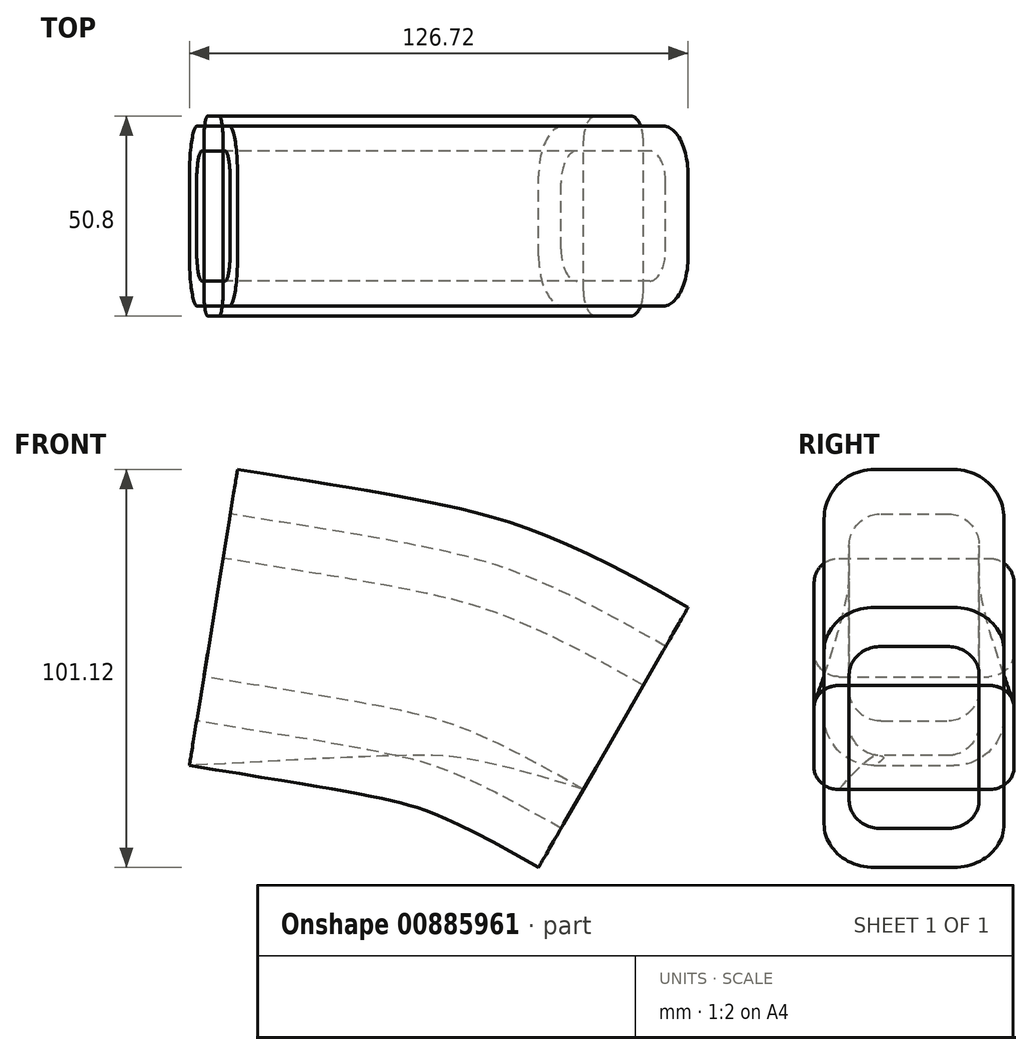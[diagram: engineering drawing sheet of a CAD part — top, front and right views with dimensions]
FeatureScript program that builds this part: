
annotation { "Feature Type Name" : "Feature", "Feature Type Description" : "" }
export const myFeature = defineFeature(function(context is Context, id is Id, definition is map)
    precondition{}
    {
        {
            var Q0;
            Q0=qCreatedBy(makeId("Right.planeOp"),FACE);
            var sketch = newSketch(context, id + "F0", { "sketchPlane" : qUnion([Q0])});
            skLineSegment(sketch, "E0", {"start": v(0, 0) * mm, "end": v(12.7, 0) * mm, "construction": true});
            skSolve(sketch);
        }
        {
            var Q0;
            Q0=qCreatedBy(makeId("Front.planeOp"),FACE);
            var sketch = newSketch(context, id + "F1", { "sketchPlane" : qUnion([Q0])});
            skLineSegment(sketch, "E1", {"start": v(0, 0) * mm, "end": v(0, 45.51) * mm});
            skFitSpline(sketch, "E2", {"points": [v(0, 0) * mm, v(-49.33, 21.4) * mm, v(-101.6, 30.48) * mm], "startDerivative": vector(-161.46, 92.87) * mm, "endDerivative": vector(-157.97, 25.7) * mm});
            skLineSegment(sketch, "E3", {"start": v(-101.6, 30.48) * mm, "end": v(0, 30.48) * mm, "construction": true});
            skPoint(sketch, "E3.endSnap0", {"position": v(0, 22.76) * mm});
            skSolve(sketch);
        }
        {
            var Q0;
            Q0=sQuery(id+"F1.wireOp",VERTEX,"E2.end");
            var Q1;
            Q1=sQuery(id+"F1.wireOp",EDGE,"E2");
            cPlane(context, id + "F2", {"entities" : qUnion([Q0, Q1]), "cplaneType" : CPlaneType.CURVE_POINT, "offset" : 25.4 * mm, "width" : 152.4 * mm, "height" : 152.4 * mm});
        }
        {
            var Q0;
            Q0=sQuery(id+"F1.wireOp",EDGE,"E2");
            var Q1;
            Q1=sQuery(id+"F1.wireOp",VERTEX,"E2.1.internal");
            cPlane(context, id + "F3", {"entities" : qUnion([Q0, Q1]), "cplaneType" : CPlaneType.CURVE_POINT, "offset" : 25.4 * mm, "width" : 152.4 * mm, "height" : 152.4 * mm});
        }
        {
            var Q0;
            Q0=sQuery(id+"F1.wireOp",EDGE,"E2");
            var Q1;
            Q1=sQuery(id+"F0.wireOp",VERTEX,"E0.start");
            cPlane(context, id + "F4", {"entities" : qUnion([Q0, Q1]), "cplaneType" : CPlaneType.CURVE_POINT, "offset" : 25.4 * mm, "width" : 152.4 * mm, "height" : 152.4 * mm});
        }
        {
            var Q0;
            Q0=qCreatedBy(id+"F4.planeOp",FACE);
            var sketch = newSketch(context, id + "F5", { "sketchPlane" : qUnion([Q0])});
            skLineSegment(sketch, "E4", {"start": v(0, 0) * mm, "end": v(0, 15.24) * mm, "construction": true});
            skLineSegment(sketch, "E5", {"start": v(0, 0) * mm, "end": v(25.4, 0) * mm, "construction": true});
            skLineSegment(sketch, "E6.bottom", {"start": v(19.05, -15.24) * mm, "end": v(-19.05, -15.24) * mm});
            skLineSegment(sketch, "E6.top", {"start": v(19.05, 15.24) * mm, "end": v(-19.05, 15.24) * mm});
            skLineSegment(sketch, "E6.left", {"start": v(25.4, -8.9) * mm, "end": v(25.4, 8.89) * mm});
            skLineSegment(sketch, "E6.right", {"start": v(-25.4, -8.89) * mm, "end": v(-25.4, 8.9) * mm});
            skPoint(sketch, "E7.visualSharp", {"position": v(25.4, -15.24) * mm});
            skArc(sketch, "E7.filletArc", {"start": v(19.05, -15.24) * mm, "mid": v(23.54, -13.38) * mm, "end": v(25.4, -8.9) * mm});
            skPoint(sketch, "E8.visualSharp", {"position": v(25.4, 15.24) * mm});
            skArc(sketch, "E8.filletArc", {"start": v(25.4, 8.89) * mm, "mid": v(23.54, 13.38) * mm, "end": v(19.05, 15.24) * mm});
            skPoint(sketch, "E9.visualSharp", {"position": v(-25.4, 15.24) * mm});
            skArc(sketch, "E9.filletArc", {"start": v(-19.05, 15.24) * mm, "mid": v(-23.54, 13.38) * mm, "end": v(-25.4, 8.9) * mm});
            skPoint(sketch, "E10.visualSharp", {"position": v(-25.4, -15.24) * mm});
            skArc(sketch, "E10.filletArc", {"start": v(-25.4, -8.89) * mm, "mid": v(-23.54, -13.38) * mm, "end": v(-19.05, -15.24) * mm});
            skSolve(sketch);
        }
        {
            var Q0;
            Q0=qCreatedBy(id+"F3.planeOp",FACE);
            var sketch = newSketch(context, id + "F6", { "sketchPlane" : qUnion([Q0])});
            skLineSegment(sketch, "E11", {"start": v(0, 10.28) * mm, "end": v(-16.51, 10.28) * mm, "construction": true});
            skLineSegment(sketch, "E12", {"start": v(0, 10.28) * mm, "end": v(0, 36.95) * mm, "construction": true});
            skLineSegment(sketch, "E13.bottom", {"start": v(8.38, 36.95) * mm, "end": v(-8.38, 36.95) * mm});
            skLineSegment(sketch, "E13.top", {"start": v(8.38, -16.4) * mm, "end": v(-8.38, -16.4) * mm});
            skLineSegment(sketch, "E13.left", {"start": v(16.5, 28.82) * mm, "end": v(16.5, -8.26) * mm});
            skLineSegment(sketch, "E13.right", {"start": v(-16.51, 28.82) * mm, "end": v(-16.51, -8.26) * mm});
            skPoint(sketch, "E14.visualSharp", {"position": v(16.5, 36.95) * mm});
            skArc(sketch, "E14.filletArc", {"start": v(16.51, 28.82) * mm, "mid": v(14.13, 34.57) * mm, "end": v(8.38, 36.95) * mm});
            skPoint(sketch, "E15.visualSharp", {"position": v(16.51, -16.4) * mm});
            skArc(sketch, "E15.filletArc", {"start": v(8.38, -16.4) * mm, "mid": v(14.13, -14.01) * mm, "end": v(16.51, -8.26) * mm});
            skPoint(sketch, "E16.visualSharp", {"position": v(-16.51, -16.4) * mm});
            skArc(sketch, "E16.filletArc", {"start": v(-16.51, -8.26) * mm, "mid": v(-14.13, -14.01) * mm, "end": v(-8.38, -16.4) * mm});
            skPoint(sketch, "E17.visualSharp", {"position": v(-16.51, 36.95) * mm});
            skArc(sketch, "E17.filletArc", {"start": v(-8.38, 36.95) * mm, "mid": v(-14.13, 34.57) * mm, "end": v(-16.51, 28.82) * mm});
            skSolve(sketch);
        }
        {
            var Q0;
            Q0=qCreatedBy(id+"F2.planeOp",FACE);
            var sketch = newSketch(context, id + "F7", { "sketchPlane" : qUnion([Q0])});
            skLineSegment(sketch, "E18", {"start": v(0, 13.77) * mm, "end": v(-22.86, 13.77) * mm, "construction": true});
            skLineSegment(sketch, "E19", {"start": v(0, 13.77) * mm, "end": v(0, 51.87) * mm, "construction": true});
            skLineSegment(sketch, "E20.bottom", {"start": v(10.16, 51.87) * mm, "end": v(-10.16, 51.87) * mm});
            skLineSegment(sketch, "E20.top", {"start": v(10.16, -24.33) * mm, "end": v(-10.16, -24.33) * mm});
            skLineSegment(sketch, "E20.left", {"start": v(22.86, 39.17) * mm, "end": v(22.86, -11.63) * mm});
            skLineSegment(sketch, "E20.right", {"start": v(-22.86, 39.17) * mm, "end": v(-22.86, -11.63) * mm});
            skPoint(sketch, "E21.visualSharp", {"position": v(22.86, 51.87) * mm});
            skArc(sketch, "E21.filletArc", {"start": v(22.86, 39.17) * mm, "mid": v(19.14, 48.15) * mm, "end": v(10.16, 51.87) * mm});
            skPoint(sketch, "E22.visualSharp", {"position": v(-22.86, 51.87) * mm});
            skArc(sketch, "E22.filletArc", {"start": v(-10.16, 51.87) * mm, "mid": v(-19.14, 48.15) * mm, "end": v(-22.86, 39.17) * mm});
            skPoint(sketch, "E23.visualSharp", {"position": v(-22.86, -24.33) * mm});
            skArc(sketch, "E23.filletArc", {"start": v(-22.86, -11.63) * mm, "mid": v(-19.14, -20.61) * mm, "end": v(-10.16, -24.33) * mm});
            skPoint(sketch, "E24.visualSharp", {"position": v(22.86, -24.33) * mm});
            skArc(sketch, "E24.filletArc", {"start": v(10.16, -24.33) * mm, "mid": v(19.14, -20.61) * mm, "end": v(22.86, -11.63) * mm});
            skSolve(sketch);
        }
        {
            var Q0;
            Q0=makeQuery(id+"F5.imprint","IMPRINT",FACE,{"disambiguationData":[TD([[makeQuery(id+"F5.imprint","IMPRINT",EDGE,{"derivedFrom":sQuery(id+"F5.wireOp",EDGE,"E6.bottom")}),-1.0]])]});
            var Q1;
            Q1=makeQuery(id+"F6.imprint","IMPRINT",FACE,{"disambiguationData":[TD([[makeQuery(id+"F6.imprint","IMPRINT",EDGE,{"derivedFrom":sQuery(id+"F6.wireOp",EDGE,"E13.bottom")}),1.0]])]});
            var Q2;
            Q2=makeQuery(id+"F7.imprint","IMPRINT",FACE,{"disambiguationData":[TD([[makeQuery(id+"F7.imprint","IMPRINT",EDGE,{"derivedFrom":sQuery(id+"F7.wireOp",EDGE,"E20.bottom")}),1.0]])]});
            var Q3;
            Q3=sQuery(id+"F1.wireOp",EDGE,"E2");
            sweep(context, id + "F8", {"profiles" : qUnion([Q0, Q1, Q2]), "path" : qUnion([Q3])});
        }
        {
            var Q0;
            Q0=sQuery(id+"F1.wireOp",EDGE,"E2");
            var Q1;
            Q1=makeQuery(id+"F5.imprint","IMPRINT",FACE,{"disambiguationData":[TD([[makeQuery(id+"F5.imprint","IMPRINT",EDGE,{"derivedFrom":sQuery(id+"F5.wireOp",EDGE,"E6.bottom")}),-1.0]])]});
            var Q2;
            Q2=makeQuery(id+"F6.imprint","IMPRINT",FACE,{"disambiguationData":[TD([[makeQuery(id+"F6.imprint","IMPRINT",EDGE,{"derivedFrom":sQuery(id+"F6.wireOp",EDGE,"E13.bottom")}),1.0]])]});
            var Q3;
            Q3=makeQuery(id+"F7.imprint","IMPRINT",FACE,{"disambiguationData":[TD([[makeQuery(id+"F7.imprint","IMPRINT",EDGE,{"derivedFrom":sQuery(id+"F7.wireOp",EDGE,"E20.bottom")}),1.0]])]});
            loft(context, id + "F9", {"addSections" : true, "spine" : qUnion([Q0]), "sectionCount" : 5, "sheetProfilesArray" : [{ "sheetProfileEntities" : qUnion([Q1]) }, { "sheetProfileEntities" : qUnion([Q2]) }, { "sheetProfileEntities" : qUnion([Q3]) }]});
        }
    });
